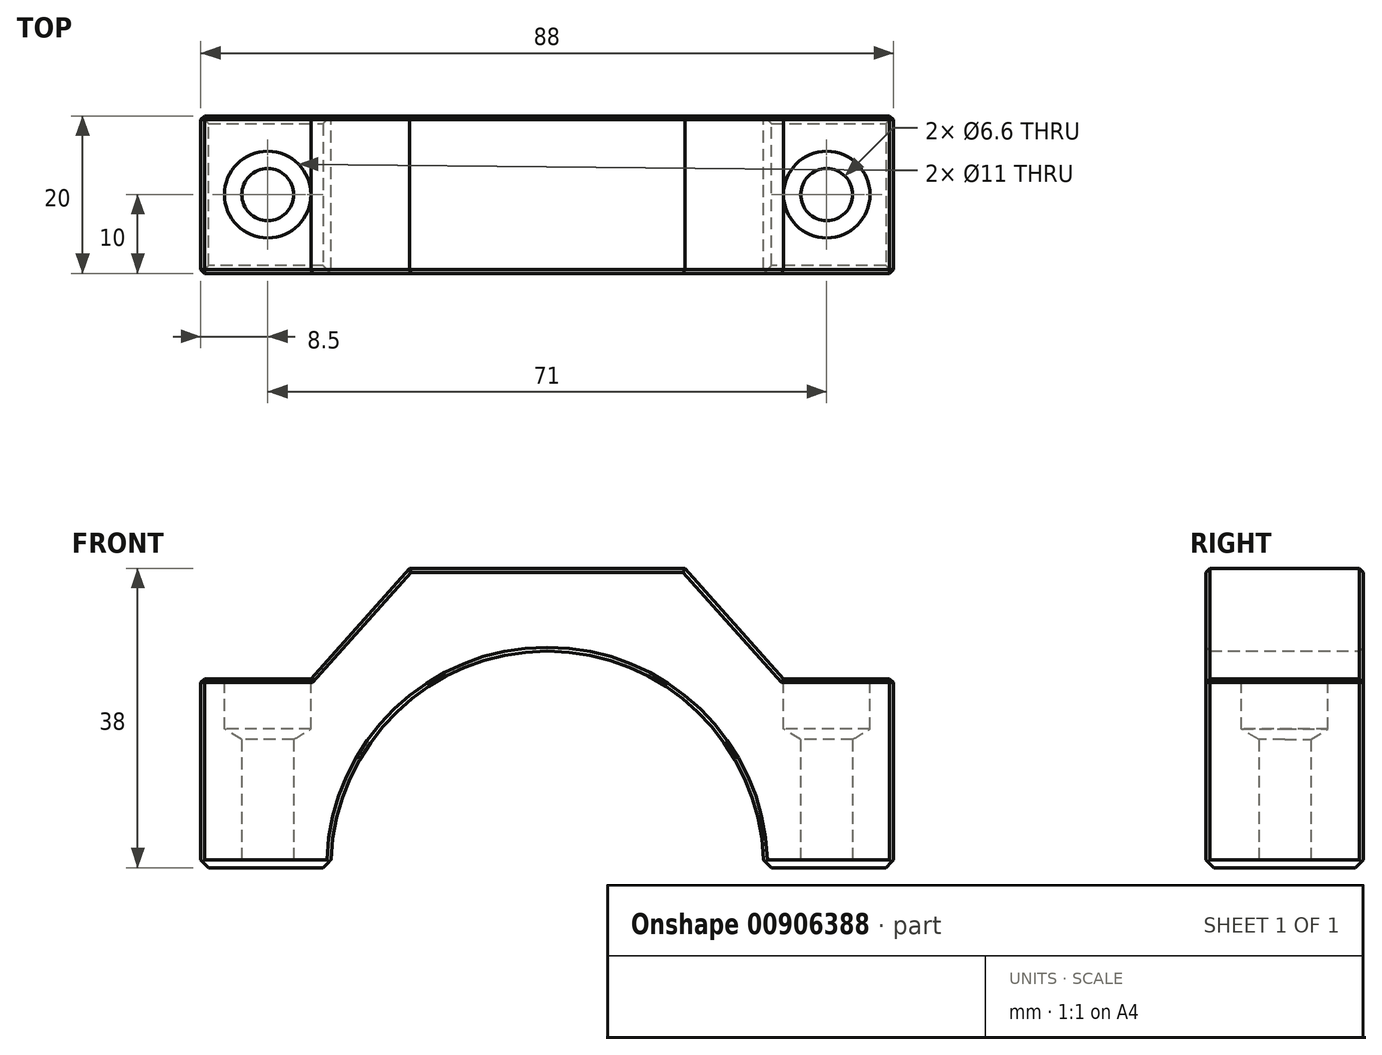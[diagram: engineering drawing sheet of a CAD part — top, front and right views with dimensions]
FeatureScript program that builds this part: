
annotation { "Feature Type Name" : "Feature", "Feature Type Description" : "" }
export const myFeature = defineFeature(function(context is Context, id is Id, definition is map)
    precondition{}
    {
        {
            var Q0;
            Q0=qCreatedBy(makeId("Front.planeOp"),FACE);
            var sketch = newSketch(context, id + "F0", { "sketchPlane" : qUnion([Q0])});
            skLineSegment(sketch, "E0", {"start": v(0, 0) * mm, "end": v(44, 0) * mm});
            skLineSegment(sketch, "E1", {"start": v(44, 0) * mm, "end": v(44, 24) * mm});
            skLineSegment(sketch, "E2", {"start": v(44, 24) * mm, "end": v(30, 24) * mm});
            skLineSegment(sketch, "E3", {"start": v(30, 24) * mm, "end": v(17.5, 38) * mm});
            skLineSegment(sketch, "E4", {"start": v(17.5, 38) * mm, "end": v(-17.5, 38) * mm});
            skLineSegment(sketch, "E5", {"start": v(-17.5, 38) * mm, "end": v(-30, 24) * mm});
            skLineSegment(sketch, "E6", {"start": v(-30, 24) * mm, "end": v(-44, 24) * mm});
            skLineSegment(sketch, "E7", {"start": v(-44, 24) * mm, "end": v(-44, 0) * mm});
            skLineSegment(sketch, "E8", {"start": v(-44, 0) * mm, "end": v(0, 0) * mm});
            skCircle(sketch, "E9", {"center": v(0, 0) * mm, "radius": 27.5 * mm});
            skSolve(sketch);
        }
        {
            var Q0;
            {var subQ0=sQuery(id+"F0.wireOp",EDGE,"E1");Q0=makeQuery(id+"F0.imprint","IMPRINT",FACE,{"disambiguationData":[TD([[makeQuery(id+"F0.imprint","IMPRINT",EDGE,{"derivedFrom":subQ0}),1.0]])]});}
            extrude(context, id + "F1", {"entities" : qUnion([Q0]), "depth" : 20 * mm, "offsetDistance" : 25 * mm});
        }
        {
            var Q0;
            Q0=makeQuery(id+"F1.opExtrude","SWEPT_FACE",FACE,{"disambiguationData":[OSD([sQuery(id+"F0.wireOp",EDGE,"E8")])]});
            var sketch = newSketch(context, id + "F2", { "sketchPlane" : qUnion([Q0])});
            skPoint(sketch, "E10", {"position": v(-35.5, 10) * mm});
            skPoint(sketch, "E11", {"position": v(35.5, 10) * mm});
            skSolve(sketch);
        }
        {
            var Q0;
            Q0=sQuery(id+"F2.wireOp",VERTEX,"E10");
            var Q1;
            Q1=sQuery(id+"F2.wireOp",VERTEX,"E11");
            var Q2;
            Q2=makeQuery(id+"F1.opExtrude","SWEPT_BODY",BODY,{"disambiguationData":[OSD([sQuery(id+"F0.wireOp",EDGE,"E0"),sQuery(id+"F0.wireOp",EDGE,"E1"),sQuery(id+"F0.wireOp",EDGE,"E2"),sQuery(id+"F0.wireOp",EDGE,"E3"),sQuery(id+"F0.wireOp",EDGE,"E4"),sQuery(id+"F0.wireOp",EDGE,"E5"),sQuery(id+"F0.wireOp",EDGE,"E6"),sQuery(id+"F0.wireOp",EDGE,"E7"),sQuery(id+"F0.wireOp",EDGE,"E8"),sQuery(id+"F0.wireOp",EDGE,"E9")])]});
            hole(context, id + "F3", {"style" : HoleStyle.SIMPLE, "endStyle" : HoleEndStyle.THROUGH, "standardTappedOrClearance" : lookupTablePath({ "fit" : "Normal", "standard" : "ISO", "size" : "M6", "type" : "Clearance" }), "standardBlindInLast" : lookupTablePath({ "fit" : "Normal", "standard" : "ISO", "size" : "M6", "type" : "Clearance" }), "holeDiameter" : 6.6 * mm, "majorDiameter" : 5 * mm, "isTappedThrough" : true, "tappedDepth" : 12 * mm, "tapClearance" : 3, "locations" : qUnion([Q0, Q1]), "scope" : qUnion([Q2])});
        }
        {
            var Q0;
            Q0=makeQuery(id+"F1.opExtrude","SWEPT_FACE",FACE,{"disambiguationData":[OSD([sQuery(id+"F0.wireOp",EDGE,"E6")])]});
            var sketch = newSketch(context, id + "F4", { "sketchPlane" : qUnion([Q0])});
            skPoint(sketch, "E12", {"position": v(-35.5, -10) * mm});
            skSolve(sketch);
        }
        {
            var Q0;
            Q0=sQuery(id+"F4.wireOp",VERTEX,"E12");
            var Q1;
            Q1=makeQuery(id+"F1.opExtrude","SWEPT_BODY",BODY,{"disambiguationData":[OSD([sQuery(id+"F0.wireOp",EDGE,"E0"),sQuery(id+"F0.wireOp",EDGE,"E1"),sQuery(id+"F0.wireOp",EDGE,"E2"),sQuery(id+"F0.wireOp",EDGE,"E3"),sQuery(id+"F0.wireOp",EDGE,"E4"),sQuery(id+"F0.wireOp",EDGE,"E5"),sQuery(id+"F0.wireOp",EDGE,"E6"),sQuery(id+"F0.wireOp",EDGE,"E7"),sQuery(id+"F0.wireOp",EDGE,"E8"),sQuery(id+"F0.wireOp",EDGE,"E9")])]});
            hole(context, id + "F5", {"style" : HoleStyle.SIMPLE, "endStyle" : HoleEndStyle.BLIND, "holeDiameter" : 11 * mm, "majorDiameter" : 5 * mm, "holeDepth" : 6.4 * mm, "isTappedThrough" : true, "tappedDepth" : 12 * mm, "tapClearance" : 3, "locations" : qUnion([Q0]), "scope" : qUnion([Q1])});
        }
        {
            var Q0;
            Q0=makeQuery(id+"F1.opExtrude","SWEPT_FACE",FACE,{"disambiguationData":[OSD([sQuery(id+"F0.wireOp",EDGE,"E2")])]});
            var sketch = newSketch(context, id + "F6", { "sketchPlane" : qUnion([Q0])});
            skPoint(sketch, "E13", {"position": v(35.5, -10) * mm});
            skSolve(sketch);
        }
        {
            var Q0;
            Q0=sQuery(id+"F6.wireOp",VERTEX,"E13");
            var Q1;
            Q1=makeQuery(id+"F1.opExtrude","SWEPT_BODY",BODY,{"disambiguationData":[OSD([sQuery(id+"F0.wireOp",EDGE,"E0"),sQuery(id+"F0.wireOp",EDGE,"E1"),sQuery(id+"F0.wireOp",EDGE,"E2"),sQuery(id+"F0.wireOp",EDGE,"E3"),sQuery(id+"F0.wireOp",EDGE,"E4"),sQuery(id+"F0.wireOp",EDGE,"E5"),sQuery(id+"F0.wireOp",EDGE,"E6"),sQuery(id+"F0.wireOp",EDGE,"E7"),sQuery(id+"F0.wireOp",EDGE,"E8"),sQuery(id+"F0.wireOp",EDGE,"E9")])]});
            hole(context, id + "F7", {"style" : HoleStyle.SIMPLE, "endStyle" : HoleEndStyle.BLIND, "holeDiameter" : 11 * mm, "majorDiameter" : 5 * mm, "holeDepth" : 6.4 * mm, "isTappedThrough" : true, "tappedDepth" : 12 * mm, "tapClearance" : 3, "locations" : qUnion([Q0]), "scope" : qUnion([Q1])});
        }
        {
            var Q0;
            Q0=makeQuery(id+"F1.opExtrude","CAP_EDGE",EDGE,{"disambiguationData":[OSD([sQuery(id+"F0.wireOp",EDGE,"E0")])],"isStart":false});
            var Q1;
            Q1=makeQuery(id+"F1.opExtrude","SWEPT_EDGE",EDGE,{"disambiguationData":[OSD([sQuery(id+"F0.wireOp",EDGE,"E0"),sQuery(id+"F0.wireOp",EDGE,"E1")])]});
            var Q2;
            Q2=makeQuery(id+"F1.opExtrude","CAP_EDGE",EDGE,{"disambiguationData":[OSD([sQuery(id+"F0.wireOp",EDGE,"E8")])],"isStart":false});
            var Q3;
            Q3=makeQuery(id+"F1.opExtrude","SWEPT_EDGE",EDGE,{"disambiguationData":[OSD([sQuery(id+"F0.wireOp",EDGE,"E8"),sQuery(id+"F0.wireOp",EDGE,"E9")])]});
            var Q4;
            Q4=makeQuery(id+"F1.opExtrude","CAP_EDGE",EDGE,{"disambiguationData":[OSD([sQuery(id+"F0.wireOp",EDGE,"E8")])],"isStart":true});
            var Q5;
            Q5=makeQuery(id+"F1.opExtrude","SWEPT_EDGE",EDGE,{"disambiguationData":[OSD([sQuery(id+"F0.wireOp",EDGE,"E7"),sQuery(id+"F0.wireOp",EDGE,"E8")])]});
            var Q6;
            Q6=makeQuery(id+"F1.opExtrude","SWEPT_EDGE",EDGE,{"disambiguationData":[OSD([sQuery(id+"F0.wireOp",EDGE,"E0"),sQuery(id+"F0.wireOp",EDGE,"E9")])]});
            var Q7;
            Q7=makeQuery(id+"F1.opExtrude","CAP_EDGE",EDGE,{"disambiguationData":[OSD([sQuery(id+"F0.wireOp",EDGE,"E0")])],"isStart":true});
            chamfer(context, id + "F8", {"entities" : qUnion([Q0, Q1, Q2, Q3, Q4, Q5, Q6, Q7]), "width" : 1 * mm, "tangentPropagation" : true});
        }
        {
            var Q0;
            Q0=makeQuery(id+"F1.opExtrude","CAP_EDGE",EDGE,{"disambiguationData":[OSD([sQuery(id+"F0.wireOp",EDGE,"E1")])],"isStart":false});
            var Q1;
            Q1=makeQuery(id+"F1.opExtrude","CAP_EDGE",EDGE,{"disambiguationData":[OSD([sQuery(id+"F0.wireOp",EDGE,"E1")])],"isStart":true});
            var Q2;
            Q2=makeQuery(id+"F1.opExtrude","SWEPT_EDGE",EDGE,{"disambiguationData":[OSD([sQuery(id+"F0.wireOp",EDGE,"E1"),sQuery(id+"F0.wireOp",EDGE,"E2")])]});
            var Q3;
            Q3=makeQuery(id+"F1.opExtrude","CAP_EDGE",EDGE,{"disambiguationData":[OSD([sQuery(id+"F0.wireOp",EDGE,"E2")])],"isStart":false});
            var Q4;
            Q4=makeQuery(id+"F1.opExtrude","CAP_EDGE",EDGE,{"disambiguationData":[OSD([sQuery(id+"F0.wireOp",EDGE,"E2")])],"isStart":true});
            var Q5;
            Q5=makeQuery(id+"F1.opExtrude","CAP_EDGE",EDGE,{"disambiguationData":[OSD([sQuery(id+"F0.wireOp",EDGE,"E3")])],"isStart":true});
            var Q6;
            Q6=makeQuery(id+"F1.opExtrude","CAP_EDGE",EDGE,{"disambiguationData":[OSD([sQuery(id+"F0.wireOp",EDGE,"E3")])],"isStart":false});
            var Q7;
            Q7=makeQuery(id+"F1.opExtrude","CAP_EDGE",EDGE,{"disambiguationData":[OSD([sQuery(id+"F0.wireOp",EDGE,"E4")])],"isStart":false});
            var Q8;
            Q8=makeQuery(id+"F1.opExtrude","CAP_EDGE",EDGE,{"disambiguationData":[OSD([sQuery(id+"F0.wireOp",EDGE,"E4")])],"isStart":true});
            var Q9;
            Q9=makeQuery(id+"F1.opExtrude","CAP_EDGE",EDGE,{"disambiguationData":[OSD([sQuery(id+"F0.wireOp",EDGE,"E5")])],"isStart":false});
            var Q10;
            Q10=makeQuery(id+"F1.opExtrude","CAP_EDGE",EDGE,{"disambiguationData":[OSD([sQuery(id+"F0.wireOp",EDGE,"E9")])],"isStart":false});
            var Q11;
            Q11=makeQuery(id+"F1.opExtrude","CAP_EDGE",EDGE,{"disambiguationData":[OSD([sQuery(id+"F0.wireOp",EDGE,"E7")])],"isStart":false});
            var Q12;
            Q12=makeQuery(id+"F1.opExtrude","CAP_EDGE",EDGE,{"disambiguationData":[OSD([sQuery(id+"F0.wireOp",EDGE,"E6")])],"isStart":false});
            var Q13;
            Q13=makeQuery(id+"F1.opExtrude","SWEPT_EDGE",EDGE,{"disambiguationData":[OSD([sQuery(id+"F0.wireOp",EDGE,"E6"),sQuery(id+"F0.wireOp",EDGE,"E7")])]});
            var Q14;
            Q14=makeQuery(id+"F1.opExtrude","CAP_EDGE",EDGE,{"disambiguationData":[OSD([sQuery(id+"F0.wireOp",EDGE,"E6")])],"isStart":true});
            var Q15;
            Q15=makeQuery(id+"F1.opExtrude","CAP_EDGE",EDGE,{"disambiguationData":[OSD([sQuery(id+"F0.wireOp",EDGE,"E9")])],"isStart":true});
            var Q16;
            Q16=makeQuery(id+"F1.opExtrude","CAP_EDGE",EDGE,{"disambiguationData":[OSD([sQuery(id+"F0.wireOp",EDGE,"E5")])],"isStart":true});
            var Q17;
            Q17=makeQuery(id+"F1.opExtrude","CAP_EDGE",EDGE,{"disambiguationData":[OSD([sQuery(id+"F0.wireOp",EDGE,"E7")])],"isStart":true});
            chamfer(context, id + "F9", {"entities" : qUnion([Q0, Q1, Q2, Q3, Q4, Q5, Q6, Q7, Q8, Q9, Q10, Q11, Q12, Q13, Q14, Q15, Q16, Q17]), "width" : 0.5 * mm, "tangentPropagation" : true});
        }
    });
